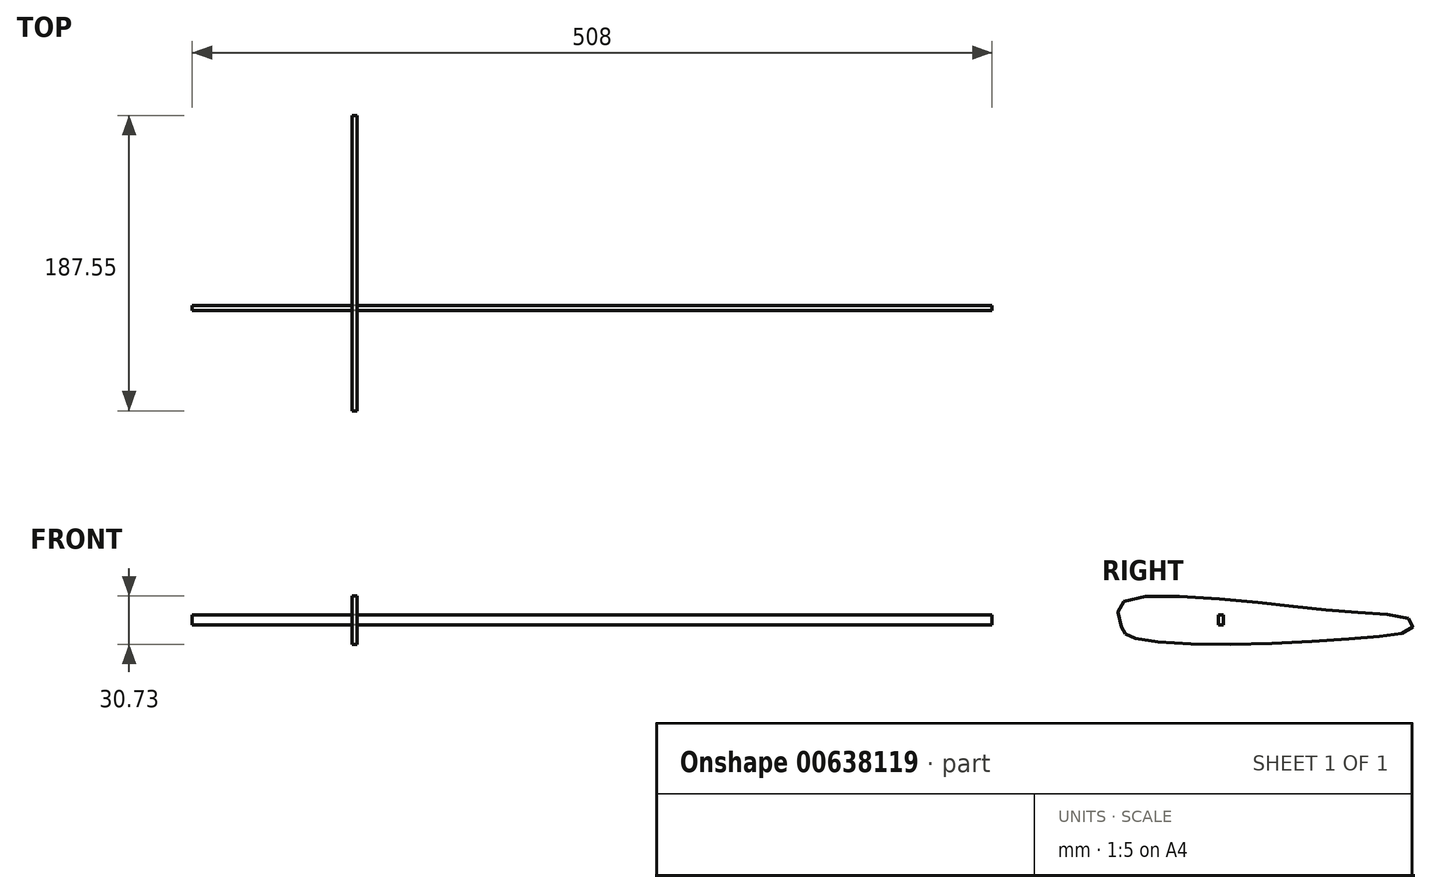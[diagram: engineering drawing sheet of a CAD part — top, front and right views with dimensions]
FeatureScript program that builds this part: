
annotation { "Feature Type Name" : "Feature", "Feature Type Description" : "" }
export const myFeature = defineFeature(function(context is Context, id is Id, definition is map)
    precondition{}
    {
        {
            var Q0;
            Q0=qCreatedBy(makeId("Right.planeOp"),FACE);
            var sketch = newSketch(context, id + "F0", { "sketchPlane" : qUnion([Q0])});
            skLineSegment(sketch, "E0.bottom", {"start": v(0, 0) * mm, "end": v(3.17, 0) * mm});
            skLineSegment(sketch, "E0.top", {"start": v(0, 6.35) * mm, "end": v(3.17, 6.35) * mm});
            skLineSegment(sketch, "E0.left", {"start": v(0, 0) * mm, "end": v(0, 6.35) * mm});
            skLineSegment(sketch, "E0.right", {"start": v(3.17, 0) * mm, "end": v(3.17, 6.35) * mm});
            skSolve(sketch);
        }
        {
            var Q0;
            Q0 = qSketchRegion(id + "F0", true);
            extrude(context, id + "F1", {"entities" : qUnion([Q0]), "depth" : 508 * mm, "offsetDistance" : 25.4 * mm});
        }
        {
            var Q0;
            Q0=qCreatedBy(makeId("Right.planeOp"),FACE);
            cPlane(context, id + "F2", {"entities" : qUnion([Q0]), "cplaneType" : CPlaneType.OFFSET, "offset" : 101.6 * mm, "width" : 152.4 * mm, "height" : 152.4 * mm});
        }
        {
            var Q0;
            Q0=qCreatedBy(id+"F2.planeOp",FACE);
            var sketch = newSketch(context, id + "F3", { "sketchPlane" : qUnion([Q0])});
            skFitSpline(sketch, "E1", {"points": [v(-59.13, -5.92) * mm, v(-60.43, -4.1) * mm, v(-63.82, 7.62) * mm, v(-58.1, 15.7) * mm, v(14.04, 15.17) * mm, v(85.91, 7.88) * mm, v(122.37, 2.93) * mm, v(122.9, -2.28) * mm, v(104.14, -7.22) * mm, v(21.6, -12.17) * mm, v(-50.54, -9.3) * mm, v(-59.13, -5.92) * mm]});
            skSolve(sketch);
        }
        {
            var Q0;
            Q0=makeQuery(id+"F3.imprint","IMPRINT",FACE,{"disambiguationData":[TD([[makeQuery(id+"F3.imprint","IMPRINT",EDGE,{"derivedFrom":sQuery(id+"F3.wireOp",EDGE,"E1")}),-1.0]])]});
            extrude(context, id + "F4", {"entities" : qUnion([Q0]), "depth" : 3.17 * mm, "offsetDistance" : 25.4 * mm});
        }
    });
